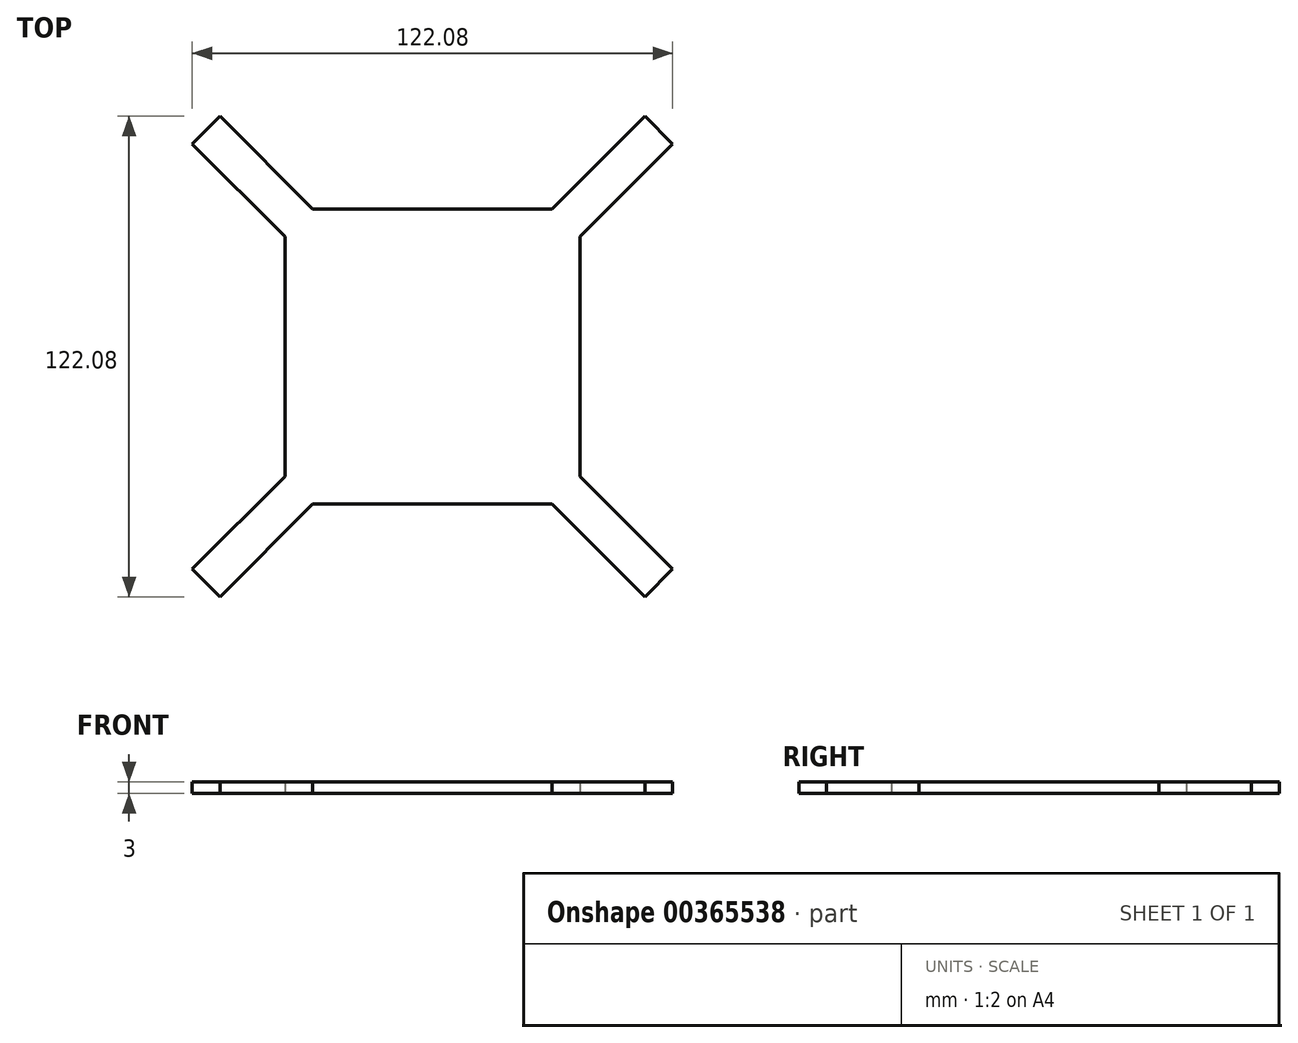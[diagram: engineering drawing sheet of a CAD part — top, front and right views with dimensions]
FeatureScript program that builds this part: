
annotation { "Feature Type Name" : "Feature", "Feature Type Description" : "" }
export const myFeature = defineFeature(function(context is Context, id is Id, definition is map)
    precondition{}
    {
        {
            var Q0;
            Q0=qCreatedBy(makeId("Top.planeOp"),FACE);
            var sketch = newSketch(context, id + "F0", { "sketchPlane" : qUnion([Q0])});
            skLineSegment(sketch, "E0", {"start": v(0, 0) * mm, "end": v(-37.5, 0) * mm, "construction": true});
            skLineSegment(sketch, "E1", {"start": v(-37.5, 0) * mm, "end": v(-37.5, -37.5) * mm, "construction": true});
            skLineSegment(sketch, "E2", {"start": v(-37.5, -37.5) * mm, "end": v(0, 0) * mm, "construction": true});
            skLineSegment(sketch, "E3", {"start": v(0, 0) * mm, "end": v(0, 37.5) * mm, "construction": true});
            skLineSegment(sketch, "E4", {"start": v(0, 37.5) * mm, "end": v(37.5, 37.5) * mm, "construction": true});
            skLineSegment(sketch, "E5", {"start": v(37.5, 37.5) * mm, "end": v(0, 0) * mm, "construction": true});
            skLineSegment(sketch, "E6.bottom", {"start": v(-37.5, -37.5) * mm, "end": v(37.5, -37.5) * mm});
            skLineSegment(sketch, "E6.top", {"start": v(-37.5, 37.5) * mm, "end": v(37.5, 37.5) * mm});
            skLineSegment(sketch, "E6.left", {"start": v(-37.5, -37.5) * mm, "end": v(-37.5, 37.5) * mm});
            skLineSegment(sketch, "E6.right", {"start": v(37.5, -37.5) * mm, "end": v(37.5, 37.5) * mm});
            skLineSegment(sketch, "E7", {"start": v(-37.5, 37.5) * mm, "end": v(-57.5, 37.5) * mm, "construction": true});
            skLineSegment(sketch, "E8", {"start": v(-37.5, 37.5) * mm, "end": v(-37.5, 57.5) * mm, "construction": true});
            skLineSegment(sketch, "E9", {"start": v(-57.5, 37.5) * mm, "end": v(-57.5, 57.5) * mm, "construction": true});
            skLineSegment(sketch, "E10", {"start": v(-57.5, 57.5) * mm, "end": v(-37.5, 57.5) * mm, "construction": true});
            skLineSegment(sketch, "E11", {"start": v(-37.5, 37.5) * mm, "end": v(-57.5, 57.5) * mm, "construction": true});
            skLineSegment(sketch, "E12", {"start": v(-57.5, 57.5) * mm, "end": v(-61.04, 53.96) * mm});
            skLineSegment(sketch, "E13", {"start": v(-57.5, 57.5) * mm, "end": v(-53.96, 61.04) * mm});
            skLineSegment(sketch, "E14", {"start": v(-61.04, 53.96) * mm, "end": v(-37.5, 30.43) * mm});
            skLineSegment(sketch, "E15", {"start": v(-53.96, 61.04) * mm, "end": v(-30.43, 37.5) * mm});
            skLineSegment(sketch, "E16.1.0", {"start": v(-53.96, -61.04) * mm, "end": v(-30.43, -37.5) * mm});
            skLineSegment(sketch, "E16.1.1", {"start": v(-57.5, -57.5) * mm, "end": v(-53.96, -61.04) * mm});
            skLineSegment(sketch, "E16.1.2", {"start": v(-57.5, -57.5) * mm, "end": v(-61.04, -53.96) * mm});
            skLineSegment(sketch, "E16.1.3", {"start": v(-61.04, -53.96) * mm, "end": v(-37.5, -30.43) * mm});
            skLineSegment(sketch, "E16.2.0", {"start": v(61.04, -53.96) * mm, "end": v(37.5, -30.43) * mm});
            skLineSegment(sketch, "E16.2.1", {"start": v(57.5, -57.5) * mm, "end": v(61.04, -53.96) * mm});
            skLineSegment(sketch, "E16.2.2", {"start": v(57.5, -57.5) * mm, "end": v(53.96, -61.04) * mm});
            skLineSegment(sketch, "E16.2.3", {"start": v(53.96, -61.04) * mm, "end": v(30.43, -37.5) * mm});
            skLineSegment(sketch, "E16.3.0", {"start": v(53.96, 61.04) * mm, "end": v(30.43, 37.5) * mm});
            skLineSegment(sketch, "E16.3.1", {"start": v(57.5, 57.5) * mm, "end": v(53.96, 61.04) * mm});
            skLineSegment(sketch, "E16.3.2", {"start": v(57.5, 57.5) * mm, "end": v(61.04, 53.96) * mm});
            skLineSegment(sketch, "E16.3.3", {"start": v(61.04, 53.96) * mm, "end": v(37.5, 30.43) * mm});
            skPoint(sketch, "E16.center", {"position": v(0, 0) * mm});
            skSolve(sketch);
        }
        {
            var Q0;
            Q0 = qSketchRegion(id + "F0", true);
            extrude(context, id + "F1", {"entities" : qUnion([Q0]), "depth" : 3 * mm});
        }
    });
